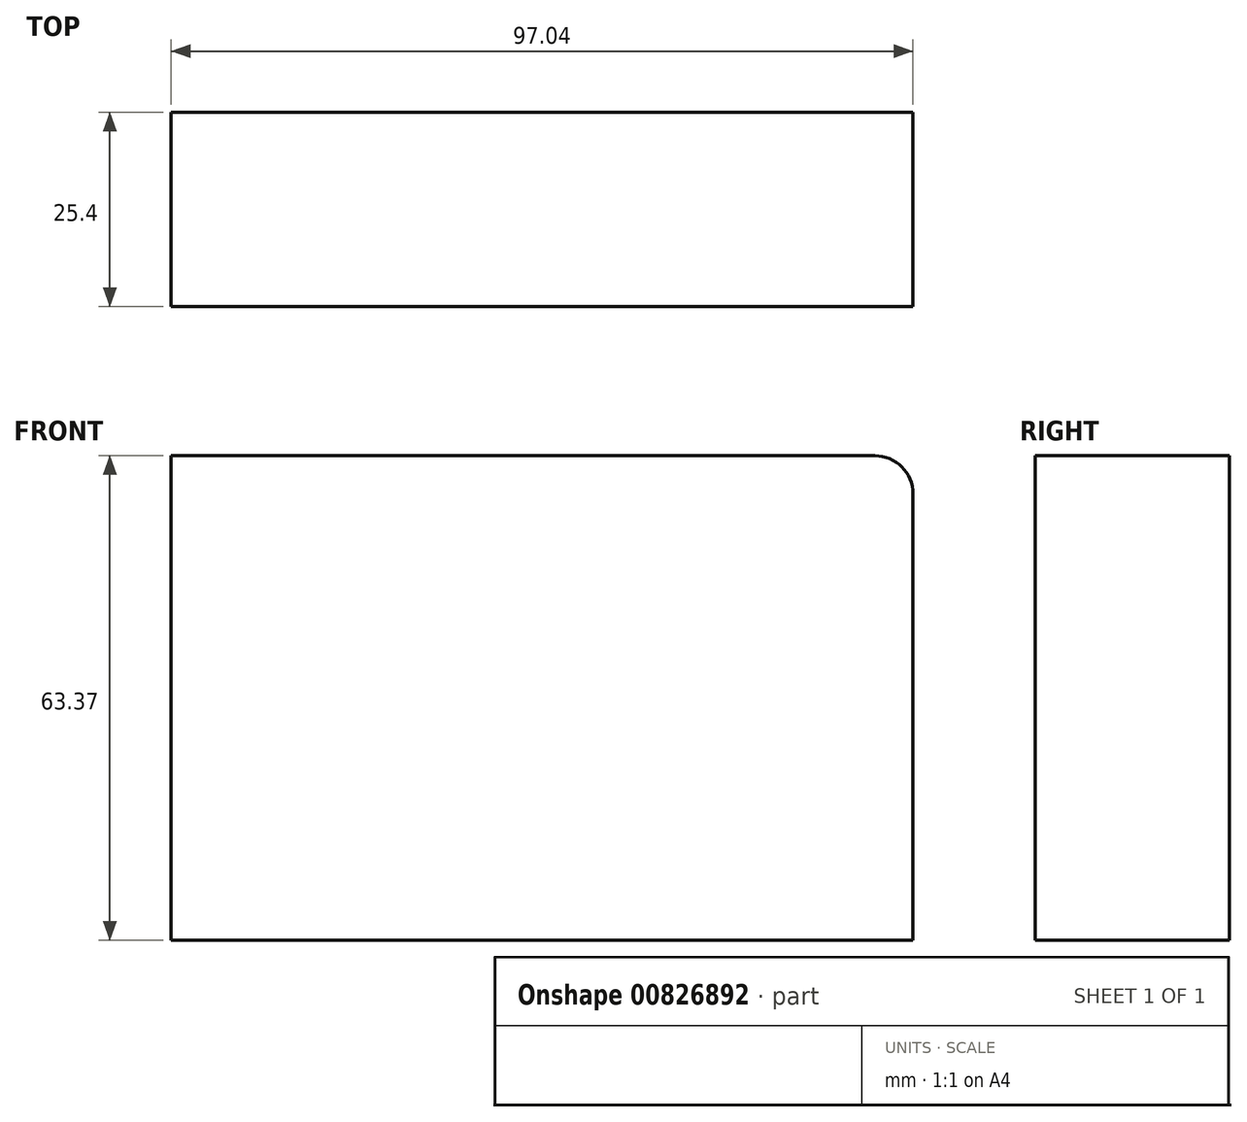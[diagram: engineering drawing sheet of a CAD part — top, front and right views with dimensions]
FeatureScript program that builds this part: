
annotation { "Feature Type Name" : "Feature", "Feature Type Description" : "" }
export const myFeature = defineFeature(function(context is Context, id is Id, definition is map)
    precondition{}
    {
        {
            var Q0;
            Q0=qCreatedBy(makeId("Front.planeOp"),FACE);
            var sketch = newSketch(context, id + "F0", { "sketchPlane" : qUnion([Q0])});
            skLineSegment(sketch, "E0.bottom", {"start": v(0, 37.88) * mm, "end": v(97.04, 37.88) * mm});
            skLineSegment(sketch, "E0.top", {"start": v(0, 101.25) * mm, "end": v(97.04, 101.25) * mm});
            skLineSegment(sketch, "E0.left", {"start": v(0, 37.88) * mm, "end": v(0, 101.25) * mm});
            skLineSegment(sketch, "E0.right", {"start": v(97.04, 37.88) * mm, "end": v(97.04, 101.25) * mm});
            skSolve(sketch);
        }
        {
            var Q0;
            Q0=makeQuery(id+"F0.imprint","IMPRINT",FACE,{"disambiguationData":[TD([[makeQuery(id+"F0.imprint","IMPRINT",EDGE,{"derivedFrom":sQuery(id+"F0.wireOp",EDGE,"E0.bottom")}),1.0]])]});
            extrude(context, id + "F1", {"entities" : qUnion([Q0]), "depth" : 25.4 * mm, "offsetDistance" : 25.4 * mm});
        }
        {
            var Q0;
            Q0=makeQuery(id+"F1.opExtrude","SWEPT_EDGE",EDGE,{"disambiguationData":[OSD([sQuery(id+"F0.wireOp",EDGE,"E0.top"),sQuery(id+"F0.wireOp",EDGE,"E0.right")])]});
            fillet(context, id + "F2", {"entities" : qUnion([Q0]), "radius" : 5 * mm, "tangentPropagation" : true, "allowEdgeOverflow" : false});
        }
    });
